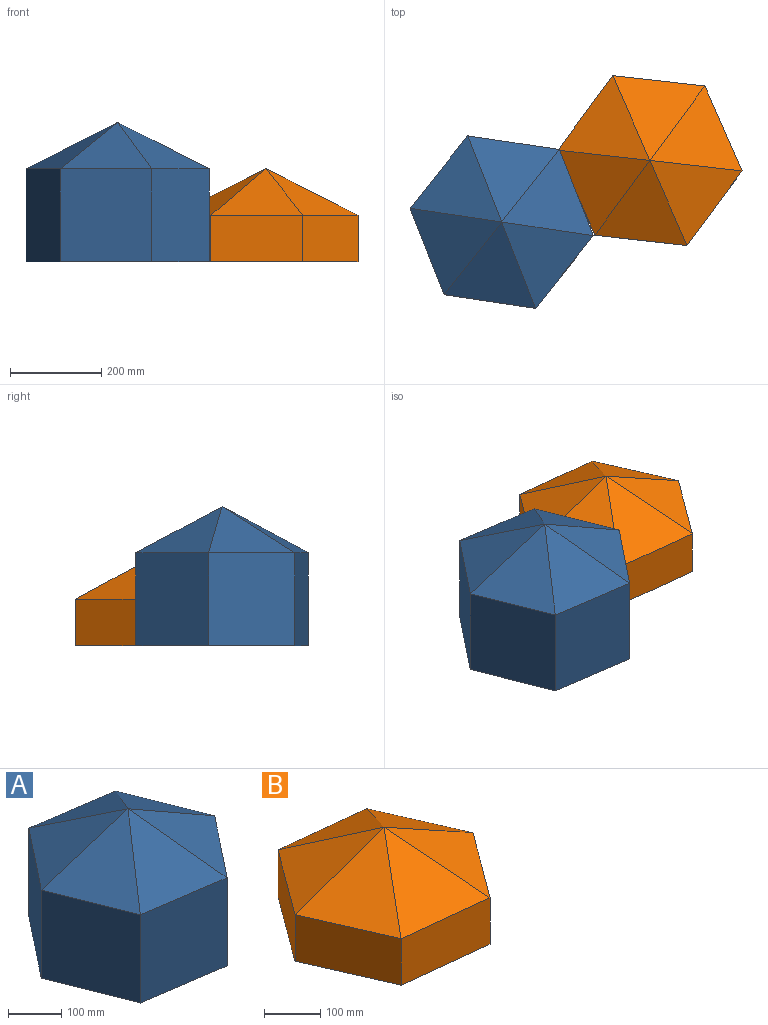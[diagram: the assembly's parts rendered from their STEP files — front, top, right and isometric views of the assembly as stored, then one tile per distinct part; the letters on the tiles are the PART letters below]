
ASSEMBLY  parts=2 mates=1
PART A: 14 faces, bbox 402x378x304.8 mm
  f0: plane 203.2x159.11mm, normal (0.78,-0.62,0), area 41290.2mm2, adj f1,f5,f7,f11
  f1: plane 203.2x189.01mm, normal (0.93,0.37,0), area 41290.2mm2, adj f0,f2,f7,f9
  f2: plane 203.2x200.99mm, normal (0.15,0.99,0), area 41290.2mm2, adj f1,f3,f7,f8
  f3: plane 203.2x159.11mm, normal (-0.78,0.62,0), area 41290.2mm2, adj f2,f4,f7,f10
  f4: plane 203.2x189.01mm, normal (-0.93,-0.37,0), area 41290.2mm2, adj f3,f5,f7,f12
  f5: plane 203.2x200.99mm, normal (-0.15,-0.99,0), area 41290.2mm2, adj f0,f4,f7,f13
  f6: plane 0.48x0.45mm, normal (0,0,1), area 0.2mm2, adj f8,f9,f10,f11,f12,f13
  f7: plane 401.98x378.02mm, normal (0,0,-1), area 107275.2mm2, adj f0,f1,f2,f3,f4,f5
  f8: plane 200.99x188.82mm, normal (0.07,0.49,0.87), area 20651.2mm2, adj f2,f6,f9,f10
  f9: plane 200.84x189.01mm, normal (0.47,0.18,0.87), area 20651.2mm2, adj f1,f6,f8,f11
  f10: plane 200.9x188.98mm, normal (-0.39,0.31,0.87), area 20651.2mm2, adj f3,f6,f8,f12
  f11: plane 200.9x188.98mm, normal (0.39,-0.31,0.87), area 20651.2mm2, adj f0,f6,f9,f13
  f12: plane 200.84x189.01mm, normal (-0.47,-0.18,0.87), area 20651.2mm2, adj f4,f6,f10,f13
  f13: plane 200.99x188.82mm, normal (-0.07,-0.49,0.87), area 20651.2mm2, adj f5,f6,f11,f12
PART B: 14 faces, bbox 403.9x372.4x203.2 mm
  f0: plane 163.54x120.6mm, normal (0.8,-0.59,0), area 20645.1mm2, adj f1,f5,f7,f11
  f1: plane 186.22x101.6mm, normal (0.92,0.4,0), area 20645.1mm2, adj f0,f2,f7,f9
  f2: plane 201.93x101.6mm, normal (0.11,0.99,0), area 20645.1mm2, adj f1,f3,f7,f8
  f3: plane 163.54x120.6mm, normal (-0.8,0.59,0), area 20645.1mm2, adj f2,f4,f7,f10
  f4: plane 186.22x101.6mm, normal (-0.92,-0.4,0), area 20645.1mm2, adj f3,f5,f7,f12
  f5: plane 201.93x101.6mm, normal (-0.11,-0.99,0), area 20645.1mm2, adj f0,f4,f7,f13
  f6: plane 0.48x0.44mm, normal (0,0,1), area 0.2mm2, adj f8,f9,f10,f11,f12,f13
  f7: plane 403.86x372.43mm, normal (0,0,-1), area 107275.2mm2, adj f0,f1,f2,f3,f4,f5
  f8: plane 201.93x186.02mm, normal (0.06,0.5,0.87), area 20651.2mm2, adj f2,f6,f9,f10
  f9: plane 201.79x186.22mm, normal (0.46,0.2,0.87), area 20651.2mm2, adj f1,f6,f8,f11
  f10: plane 201.83x186.19mm, normal (-0.4,0.3,0.87), area 20651.2mm2, adj f3,f6,f8,f12
  f11: plane 201.83x186.19mm, normal (0.4,-0.3,0.87), area 20651.2mm2, adj f0,f6,f9,f13
  f12: plane 201.79x186.22mm, normal (-0.46,-0.2,0.87), area 20651.2mm2, adj f4,f6,f10,f13
  f13: plane 201.93x186.02mm, normal (-0.06,-0.5,0.87), area 20651.2mm2, adj f5,f6,f11,f12
PLACE A t=(-203.68,-84.65,-2.86)mm
PLACE B t=(121.28,50.39,-2.86)mm
MATE fastened B.f7 <-> A.f7  axis (0,0,-1) through (-39.99,-20.04,-2.86)mm
